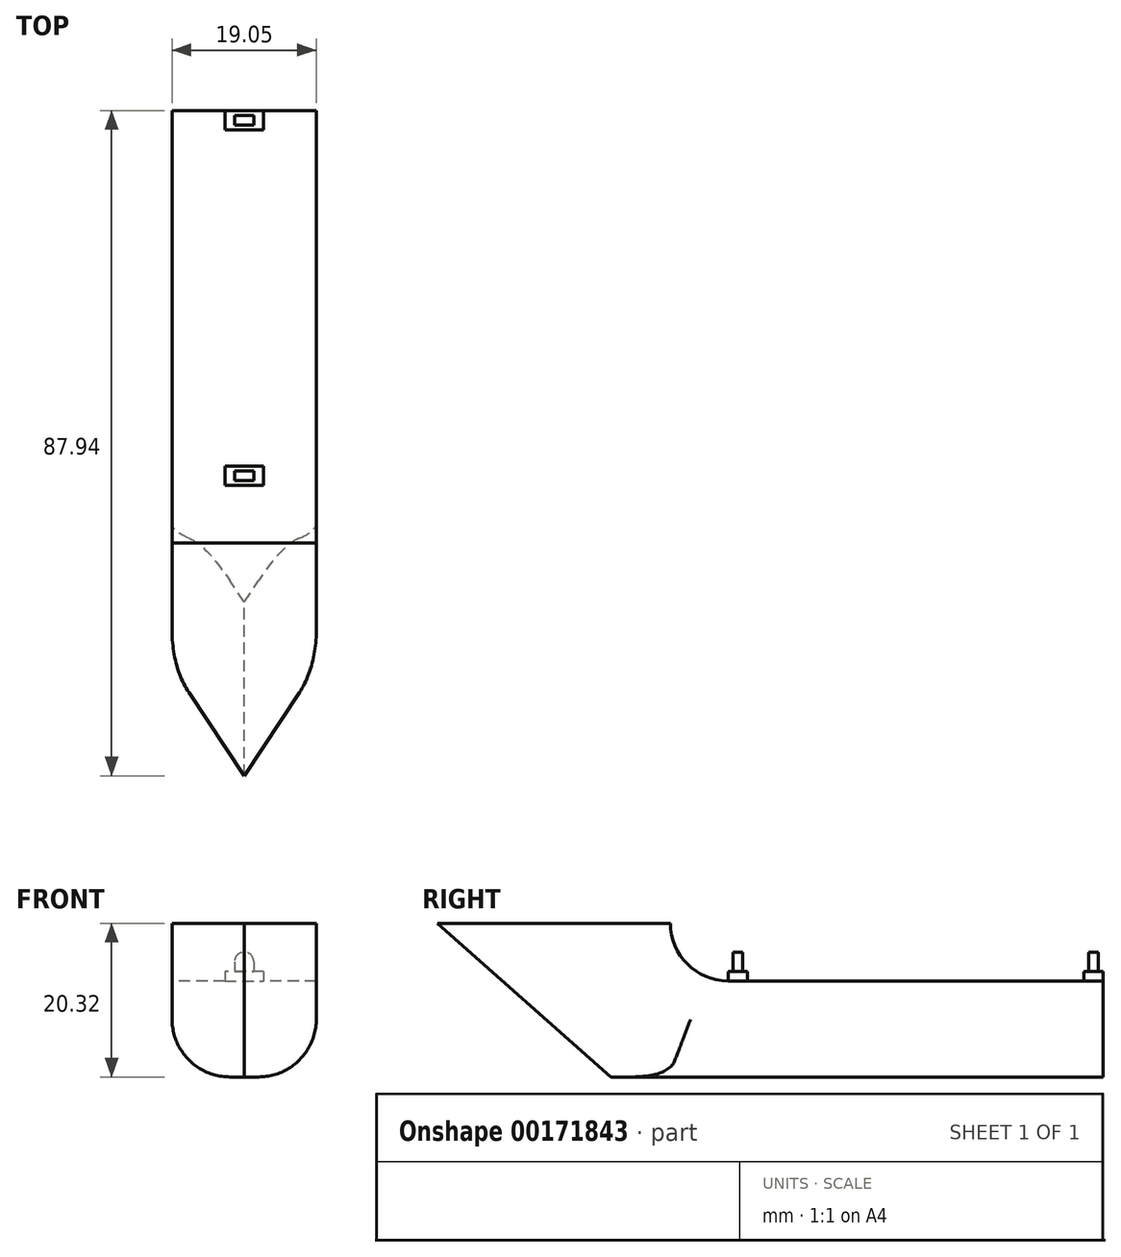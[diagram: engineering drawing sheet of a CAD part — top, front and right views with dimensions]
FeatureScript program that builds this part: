
annotation { "Feature Type Name" : "Feature", "Feature Type Description" : "" }
export const myFeature = defineFeature(function(context is Context, id is Id, definition is map)
    precondition{}
    {
        {
            var Q0;
            Q0=qCreatedBy(makeId("Right.planeOp"),FACE);
            var sketch = newSketch(context, id + "F0", { "sketchPlane" : qUnion([Q0])});
            skLineSegment(sketch, "E0", {"start": v(0, 0) * mm, "end": v(-22.93, 20.32) * mm});
            skLineSegment(sketch, "E1", {"start": v(-22.93, 20.32) * mm, "end": v(8.82, 20.32) * mm});
            skLineSegment(sketch, "E2", {"start": v(8.82, 20.32) * mm, "end": v(8.82, 12.7) * mm});
            skLineSegment(sketch, "E3", {"start": v(8.82, 12.7) * mm, "end": v(65.97, 12.7) * mm});
            skLineSegment(sketch, "E4", {"start": v(65.97, 12.7) * mm, "end": v(65.97, 0) * mm});
            skLineSegment(sketch, "E5", {"start": v(65.97, 0) * mm, "end": v(0, 0) * mm});
            skSolve(sketch);
        }
        {
            var Q0;
            Q0=makeQuery(id+"F0.imprint","IMPRINT",FACE,{"disambiguationData":[TD([[makeQuery(id+"F0.imprint","IMPRINT",EDGE,{"derivedFrom":sQuery(id+"F0.wireOp",EDGE,"E0")}),-1.0]])]});
            extrude(context, id + "F1", {"entities" : qUnion([Q0]), "depth" : 19.05 * mm});
        }
        {
            var Q0;
            Q0=makeQuery(id+"F1.opExtrude","CAP_EDGE",EDGE,{"disambiguationData":[OSD([sQuery(id+"F0.wireOp",EDGE,"E0")])],"isStart":false});
            var Q1;
            Q1=makeQuery(id+"F1.opExtrude","CAP_EDGE",EDGE,{"disambiguationData":[OSD([sQuery(id+"F0.wireOp",EDGE,"E0")])],"isStart":true});
            chamfer(context, id + "F2", {"entities" : qUnion([Q0, Q1]), "width" : 10.16 * mm, "tangentPropagation" : true});
        }
        {
            var Q0;
            {var subQ0=sQuery(id+"F0.wireOp",EDGE,"E0");Q0=makeQuery(id+"F2.opChamfer","BLEND_EDGE",EDGE,{"blendedFrom":[makeQuery(id+"F1.opExtrude","CAP_EDGE",EDGE,{"disambiguationData":[OSD([subQ0])],"isStart":true}),makeQuery(id+"F1.opExtrude","CAP_FACE",FACE,{"disambiguationData":[OSD([subQ0,sQuery(id+"F0.wireOp",EDGE,"E1"),sQuery(id+"F0.wireOp",EDGE,"E2"),sQuery(id+"F0.wireOp",EDGE,"E3"),sQuery(id+"F0.wireOp",EDGE,"E4"),sQuery(id+"F0.wireOp",EDGE,"E5")])],"isStart":true})],"blendedInto":[makeQuery(id+"F1.opExtrude","CAP_FACE",FACE,{"disambiguationData":[OSD([subQ0,sQuery(id+"F0.wireOp",EDGE,"E1"),sQuery(id+"F0.wireOp",EDGE,"E2"),sQuery(id+"F0.wireOp",EDGE,"E3"),sQuery(id+"F0.wireOp",EDGE,"E4"),sQuery(id+"F0.wireOp",EDGE,"E5")])],"isStart":true})]});}
            var Q1;
            Q1=makeQuery(id+"F1.opExtrude","CAP_EDGE",EDGE,{"disambiguationData":[OSD([sQuery(id+"F0.wireOp",EDGE,"E5")])],"isStart":true});
            var Q2;
            Q2=makeQuery(id+"F1.opExtrude","CAP_EDGE",EDGE,{"disambiguationData":[OSD([sQuery(id+"F0.wireOp",EDGE,"E5")])],"isStart":false});
            var Q3;
            {var subQ0=sQuery(id+"F0.wireOp",EDGE,"E0");Q3=makeQuery(id+"F2.opChamfer","BLEND_EDGE",EDGE,{"blendedFrom":[makeQuery(id+"F1.opExtrude","CAP_EDGE",EDGE,{"disambiguationData":[OSD([subQ0])],"isStart":false}),makeQuery(id+"F1.opExtrude","CAP_FACE",FACE,{"disambiguationData":[OSD([subQ0,sQuery(id+"F0.wireOp",EDGE,"E1"),sQuery(id+"F0.wireOp",EDGE,"E2"),sQuery(id+"F0.wireOp",EDGE,"E3"),sQuery(id+"F0.wireOp",EDGE,"E4"),sQuery(id+"F0.wireOp",EDGE,"E5")])],"isStart":false})],"blendedInto":[makeQuery(id+"F1.opExtrude","CAP_FACE",FACE,{"disambiguationData":[OSD([subQ0,sQuery(id+"F0.wireOp",EDGE,"E1"),sQuery(id+"F0.wireOp",EDGE,"E2"),sQuery(id+"F0.wireOp",EDGE,"E3"),sQuery(id+"F0.wireOp",EDGE,"E4"),sQuery(id+"F0.wireOp",EDGE,"E5")])],"isStart":false})]});}
            var Q4;
            Q4=makeQuery(id+"F1.opExtrude","SWEPT_EDGE",EDGE,{"disambiguationData":[OSD([sQuery(id+"F0.wireOp",EDGE,"E2"),sQuery(id+"F0.wireOp",EDGE,"E3")])]});
            fillet(context, id + "F3", {"entities" : qUnion([Q0, Q1, Q2, Q3, Q4]), "radius" : 7.62 * mm, "tangentPropagation" : true, "allowEdgeOverflow" : false});
        }
        {
            var Q0;
            Q0=makeQuery(id+"F1.opExtrude","SWEPT_FACE",FACE,{"disambiguationData":[OSD([sQuery(id+"F0.wireOp",EDGE,"E3")])]});
            var sketch = newSketch(context, id + "F4", { "sketchPlane" : qUnion([Q0])});
            skLineSegment(sketch, "E6.bottom", {"start": v(6.98, 16.44) * mm, "end": v(12.06, 16.44) * mm});
            skLineSegment(sketch, "E6.top", {"start": v(6.98, 18.98) * mm, "end": v(12.06, 18.98) * mm});
            skLineSegment(sketch, "E6.left", {"start": v(6.98, 16.44) * mm, "end": v(6.98, 18.98) * mm});
            skLineSegment(sketch, "E6.right", {"start": v(12.06, 16.44) * mm, "end": v(12.06, 18.98) * mm});
            skLineSegment(sketch, "E7.bottom", {"start": v(6.98, 65.97) * mm, "end": v(12.06, 65.97) * mm});
            skLineSegment(sketch, "E7.top", {"start": v(6.98, 63.43) * mm, "end": v(12.06, 63.43) * mm});
            skLineSegment(sketch, "E7.left", {"start": v(6.98, 65.97) * mm, "end": v(6.98, 63.43) * mm});
            skLineSegment(sketch, "E7.right", {"start": v(12.06, 65.97) * mm, "end": v(12.06, 63.43) * mm});
            skSolve(sketch);
        }
        {
            var Q0;
            Q0=makeQuery(id+"F4.imprint","IMPRINT",FACE,{"disambiguationData":[TD([[makeQuery(id+"F4.imprint","IMPRINT",EDGE,{"derivedFrom":sQuery(id+"F4.wireOp",EDGE,"E6.bottom")}),1.0]])]});
            var sketch = newSketch(context, id + "F5", { "sketchPlane" : qUnion([Q0])});
            skLineSegment(sketch, "E8.bottom", {"start": v(8.25, 18.34) * mm, "end": v(10.8, 18.34) * mm});
            skLineSegment(sketch, "E8.top", {"start": v(8.25, 17.07) * mm, "end": v(10.8, 17.07) * mm});
            skLineSegment(sketch, "E8.left", {"start": v(8.25, 18.34) * mm, "end": v(8.25, 17.07) * mm});
            skLineSegment(sketch, "E8.right", {"start": v(10.8, 18.34) * mm, "end": v(10.8, 17.07) * mm});
            skLineSegment(sketch, "E9.bottom", {"start": v(8.25, 65.33) * mm, "end": v(10.8, 65.33) * mm});
            skLineSegment(sketch, "E9.top", {"start": v(8.25, 64.06) * mm, "end": v(10.8, 64.06) * mm});
            skLineSegment(sketch, "E9.left", {"start": v(8.25, 65.33) * mm, "end": v(8.25, 64.06) * mm});
            skLineSegment(sketch, "E9.right", {"start": v(10.8, 65.33) * mm, "end": v(10.8, 64.06) * mm});
            skSolve(sketch);
        }
        {
            var Q0;
            Q0 = qSketchRegion(id + "F5", true);
            extrude(context, id + "F6", {"entities" : qUnion([Q0]), "operationType" : NewBodyOperationType.ADD, "depth" : 3.8 * mm});
        }
        {
            var Q0;
            Q0 = qSketchRegion(id + "F4", true);
            extrude(context, id + "F7", {"entities" : qUnion([Q0]), "operationType" : NewBodyOperationType.ADD, "depth" : 1.27 * mm});
        }
        {
            var Q0;
            Q0=makeQuery(id+"F6.opExtrude","CAP_EDGE",EDGE,{"disambiguationData":[OSD([sQuery(id+"F5.wireOp",EDGE,"E8.right")])],"isStart":false});
            var Q1;
            Q1=makeQuery(id+"F6.opExtrude","CAP_EDGE",EDGE,{"disambiguationData":[OSD([sQuery(id+"F5.wireOp",EDGE,"E8.left")])],"isStart":false});
            var Q2;
            Q2=makeQuery(id+"F6.opExtrude","CAP_EDGE",EDGE,{"disambiguationData":[OSD([sQuery(id+"F5.wireOp",EDGE,"E9.left")])],"isStart":false});
            var Q3;
            Q3=makeQuery(id+"F6.opExtrude","CAP_EDGE",EDGE,{"disambiguationData":[OSD([sQuery(id+"F5.wireOp",EDGE,"E9.right")])],"isStart":false});
            fillet(context, id + "F8", {"entities" : qUnion([Q0, Q1, Q2, Q3]), "radius" : 1.27 * mm, "tangentPropagation" : true, "allowEdgeOverflow" : false});
        }
    });
